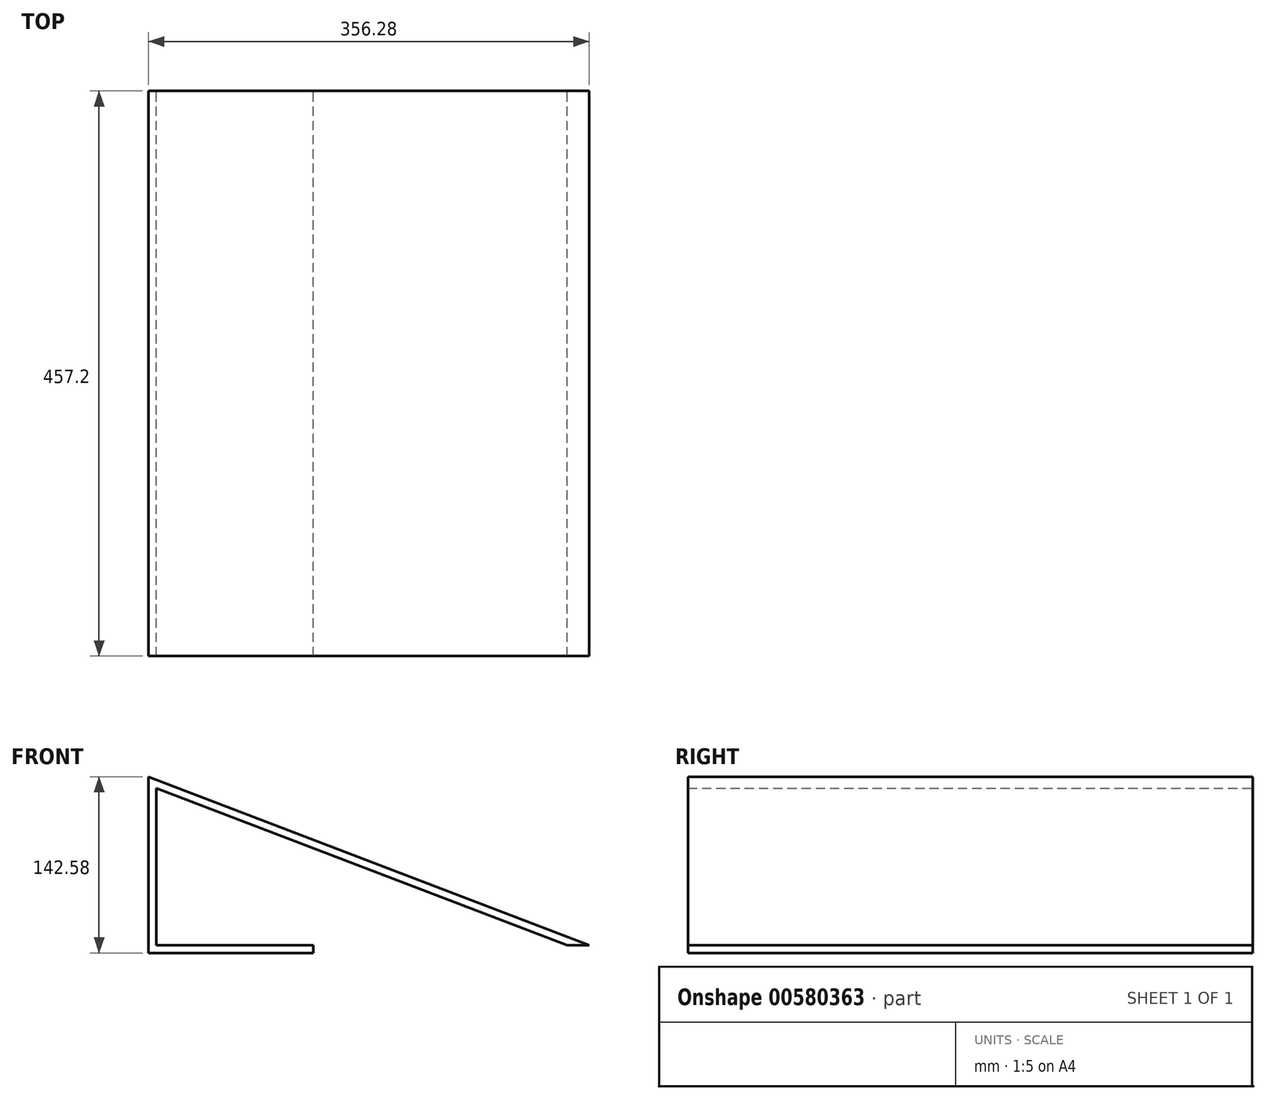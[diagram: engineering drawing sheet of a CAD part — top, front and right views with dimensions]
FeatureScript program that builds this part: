
annotation { "Feature Type Name" : "Feature", "Feature Type Description" : "" }
export const myFeature = defineFeature(function(context is Context, id is Id, definition is map)
    precondition{}
    {
        {
            var Q0;
            Q0=qCreatedBy(makeId("Front.planeOp"),FACE);
            var sketch = newSketch(context, id + "F0", { "sketchPlane" : qUnion([Q0])});
            skLineSegment(sketch, "E0", {"start": v(-127, -38.98) * mm, "end": v(-127, 88.02) * mm});
            skLineSegment(sketch, "E1", {"start": v(-127, 88.02) * mm, "end": v(205.15, -38.98) * mm});
            skLineSegment(sketch, "E2", {"start": v(-127, -38.98) * mm, "end": v(205.15, -38.98) * mm});
            skSolve(sketch);
        }
        {
            var Q0;
            Q0=makeQuery(id+"F0.imprint","IMPRINT",FACE,{"disambiguationData":[TD([[makeQuery(id+"F0.imprint","IMPRINT",EDGE,{"derivedFrom":sQuery(id+"F0.wireOp",EDGE,"E0")}),-1.0]])]});
            extrude(context, id + "F1", {"entities" : qUnion([Q0]), "depth" : 457.2 * mm, "offsetDistance" : 25.4 * mm});
        }
        {
            var Q0;
            Q0=makeQuery(id+"F1.opExtrude","CAP_FACE",FACE,{"disambiguationData":[OSD([sQuery(id+"F0.wireOp",EDGE,"E0"),sQuery(id+"F0.wireOp",EDGE,"E1"),sQuery(id+"F0.wireOp",EDGE,"E2")])],"isStart":false});
            var Q1;
            Q1=makeQuery(id+"F1.opExtrude","CAP_FACE",FACE,{"disambiguationData":[OSD([sQuery(id+"F0.wireOp",EDGE,"E0"),sQuery(id+"F0.wireOp",EDGE,"E1"),sQuery(id+"F0.wireOp",EDGE,"E2")])],"isStart":true});
            shell(context, id + "F2", {"entities" : qUnion([Q0, Q1]), "thickness" : 6.35 * mm, "oppositeDirection" : true});
        }
        {
            var Q0;
            Q0=makeQuery(id+"F1.opExtrude","SWEPT_FACE",FACE,{"disambiguationData":[OSD([sQuery(id+"F0.wireOp",EDGE,"E2")])]});
            var sketch = newSketch(context, id + "F3", { "sketchPlane" : qUnion([Q0])});
            skLineSegment(sketch, "E3", {"start": v(0, 457.2) * mm, "end": v(0, 0) * mm});
            skLineSegment(sketch, "E4", {"start": v(0, 457.2) * mm, "end": v(239.54, 457.2) * mm});
            skLineSegment(sketch, "E5", {"start": v(239.54, 457.2) * mm, "end": v(239.54, 0) * mm});
            skLineSegment(sketch, "E6", {"start": v(239.54, 0) * mm, "end": v(0, 0) * mm});
            skSolve(sketch);
        }
        {
            var Q0;
            Q0=makeQuery(id+"F3.imprint","IMPRINT",FACE,{"disambiguationData":[TD([[makeQuery(id+"F3.imprint","IMPRINT",EDGE,{"derivedFrom":sQuery(id+"F3.wireOp",EDGE,"E3")}),1.0]])]});
            extrude(context, id + "F4", {"entities" : qUnion([Q0]), "operationType" : NewBodyOperationType.REMOVE, "oppositeDirection" : true, "depth" : 6.35 * mm, "offsetDistance" : 25.4 * mm});
        }
    });
